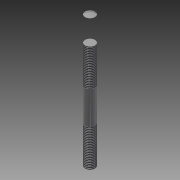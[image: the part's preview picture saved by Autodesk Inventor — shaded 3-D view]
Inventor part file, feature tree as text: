
AUTODESK INVENTOR PART (.ipt)
format: ipt  version: 2015 (Build 190159000, 159)  size: 111,616 bytes
history: native  units: mm
features: other x2, thread x2, sketch x2, extrude x1
ambient origin geometry x8: Origin, YZ Plane, XZ Plane, XY Plane, X Axis, Y Axis, Z Axis, Center Point
bodies: Body1 (feature_tree)
feature tree (7):
  other  "Bryła1"
  extrude  "Oś"  Depth=12.0mm
  thread  "Gwint1"
  thread  "Gwint2"
  other  "Obrót zakończeń"
  sketch  "Szkic1"
  sketch  "Szkic4"
